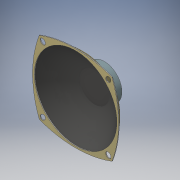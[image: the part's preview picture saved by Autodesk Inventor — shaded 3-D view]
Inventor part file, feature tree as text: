
AUTODESK INVENTOR PART (.ipt)
format: ipt  version: 2016 (Build 200138000, 138)  size: 215,552 bytes
history: native  units: in
note: dims shown in document units (in); Inventor stores cm internally (conversion verified against a paired STEP export)
features: sketch x3, extrude x2, plane x2, revolve x1
ambient origin geometry x8: Origin, YZ Plane, XZ Plane, XY Plane, X Axis, Y Axis, Z Axis, Center Point
bodies: Solid1 (feature_tree)
feature tree (8):
  extrude  "Extrusion1"  Depth=1.0in
  plane  "Work Plane1"
  extrude  "Extrusion2"  Depth=0.35in TaperAngle=0.0deg
  plane  "Work Plane2"
  revolve  "Revolution1"  [1 undecoded]
  sketch  "Sketch1"  dims[d16=0.025in d17=0.0in d18=1.0in]
  sketch  "Sketch2"  dims[d19=1.25in d20=0.35in d21=0.0in]
  sketch  "Sketch6"  dims[d22=-1.53in d23=0.1in d24=0.1in d25=90.0deg]
note: 1 required parameter value undecoded (feature->parameter linkage not recoverable at this tier; creation-order binding heuristic only, values carry confidence <= 0.55)
